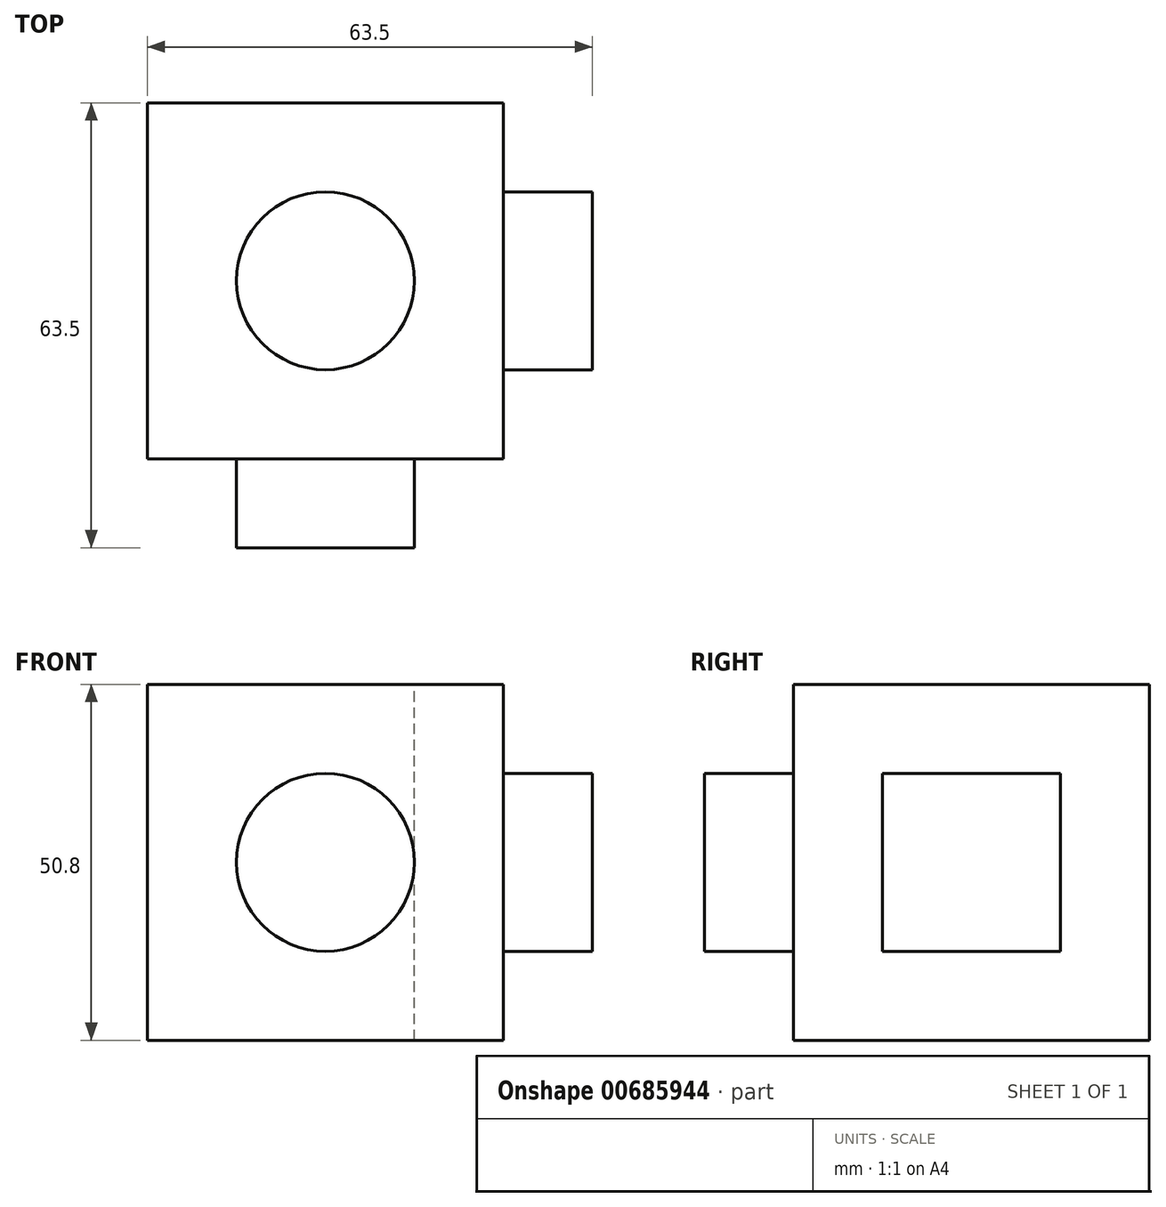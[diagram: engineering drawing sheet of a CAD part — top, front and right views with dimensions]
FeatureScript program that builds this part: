
annotation { "Feature Type Name" : "Feature", "Feature Type Description" : "" }
export const myFeature = defineFeature(function(context is Context, id is Id, definition is map)
    precondition{}
    {
        {
            var Q0;
            Q0=qCreatedBy(makeId("Top.planeOp"),FACE);
            var sketch = newSketch(context, id + "F0", { "sketchPlane" : qUnion([Q0])});
            skLineSegment(sketch, "E0.bottom", {"start": v(0, -1.43) * mm, "end": v(50.8, -1.43) * mm});
            skLineSegment(sketch, "E0.top", {"start": v(0, 49.37) * mm, "end": v(50.8, 49.37) * mm});
            skLineSegment(sketch, "E0.left", {"start": v(0, -1.43) * mm, "end": v(0, 49.37) * mm});
            skLineSegment(sketch, "E0.right", {"start": v(50.8, -1.43) * mm, "end": v(50.8, 49.37) * mm});
            skSolve(sketch);
        }
        {
            var Q0;
            Q0=makeQuery(id+"F0.imprint","IMPRINT",FACE,{"disambiguationData":[TD([[makeQuery(id+"F0.imprint","IMPRINT",EDGE,{"derivedFrom":sQuery(id+"F0.wireOp",EDGE,"E0.bottom")}),1.0]])]});
            extrude(context, id + "F1", {"entities" : qUnion([Q0]), "depth" : 50.8 * mm, "offsetDistance" : 25.4 * mm});
        }
        {
            var Q0;
            Q0=makeQuery(id+"F1.opExtrude","SWEPT_FACE",FACE,{"disambiguationData":[OSD([sQuery(id+"F0.wireOp",EDGE,"E0.right")])]});
            var sketch = newSketch(context, id + "F2", { "sketchPlane" : qUnion([Q0])});
            skLineSegment(sketch, "E1.bottom", {"start": v(11.27, 38.1) * mm, "end": v(36.67, 38.1) * mm});
            skLineSegment(sketch, "E1.top", {"start": v(11.27, 12.7) * mm, "end": v(36.67, 12.7) * mm});
            skLineSegment(sketch, "E1.left", {"start": v(11.27, 38.1) * mm, "end": v(11.27, 12.7) * mm});
            skLineSegment(sketch, "E1.right", {"start": v(36.67, 38.1) * mm, "end": v(36.67, 12.7) * mm});
            skSolve(sketch);
        }
        {
            var Q0;
            Q0=makeQuery(id+"F2.imprint","IMPRINT",FACE,{"disambiguationData":[TD([[makeQuery(id+"F2.imprint","IMPRINT",EDGE,{"derivedFrom":sQuery(id+"F2.wireOp",EDGE,"E1.bottom")}),-1.0]])]});
            extrude(context, id + "F3", {"entities" : qUnion([Q0]), "operationType" : NewBodyOperationType.ADD, "depth" : 12.7 * mm, "offsetDistance" : 25.4 * mm});
        }
        {
            var Q0;
            Q0=makeQuery(id+"F1.opExtrude","SWEPT_FACE",FACE,{"disambiguationData":[OSD([sQuery(id+"F0.wireOp",EDGE,"E0.bottom")])]});
            var sketch = newSketch(context, id + "F4", { "sketchPlane" : qUnion([Q0])});
            skCircle(sketch, "E2", {"center": v(25.4, 25.4) * mm, "radius": 12.7 * mm});
            skSolve(sketch);
        }
        {
            var Q0;
            Q0=makeQuery(id+"F4.imprint","IMPRINT",FACE,{"disambiguationData":[TD([[makeQuery(id+"F4.imprint","IMPRINT",EDGE,{"derivedFrom":sQuery(id+"F4.wireOp",EDGE,"E2")}),1.0]])]});
            extrude(context, id + "F5", {"entities" : qUnion([Q0]), "operationType" : NewBodyOperationType.ADD, "depth" : 12.7 * mm, "offsetDistance" : 25.4 * mm});
        }
        {
            var Q0;
            Q0=makeQuery(id+"F1.opExtrude","CAP_FACE",FACE,{"disambiguationData":[OSD([sQuery(id+"F0.wireOp",EDGE,"E0.bottom"),sQuery(id+"F0.wireOp",EDGE,"E0.top"),sQuery(id+"F0.wireOp",EDGE,"E0.left"),sQuery(id+"F0.wireOp",EDGE,"E0.right")])],"isStart":false});
            var sketch = newSketch(context, id + "F6", { "sketchPlane" : qUnion([Q0])});
            skCircle(sketch, "E3", {"center": v(25.4, 23.97) * mm, "radius": 12.7 * mm});
            skSolve(sketch);
        }
        {
            var Q0;
            Q0=makeQuery(id+"F6.imprint","IMPRINT",FACE,{"disambiguationData":[TD([[makeQuery(id+"F6.imprint","IMPRINT",EDGE,{"derivedFrom":sQuery(id+"F6.wireOp",EDGE,"E3")}),1.0]])]});
            extrude(context, id + "F7", {"entities" : qUnion([Q0]), "operationType" : NewBodyOperationType.REMOVE, "oppositeDirection" : true, "depth" : 50.8 * mm, "offsetDistance" : 25.4 * mm});
        }
    });
